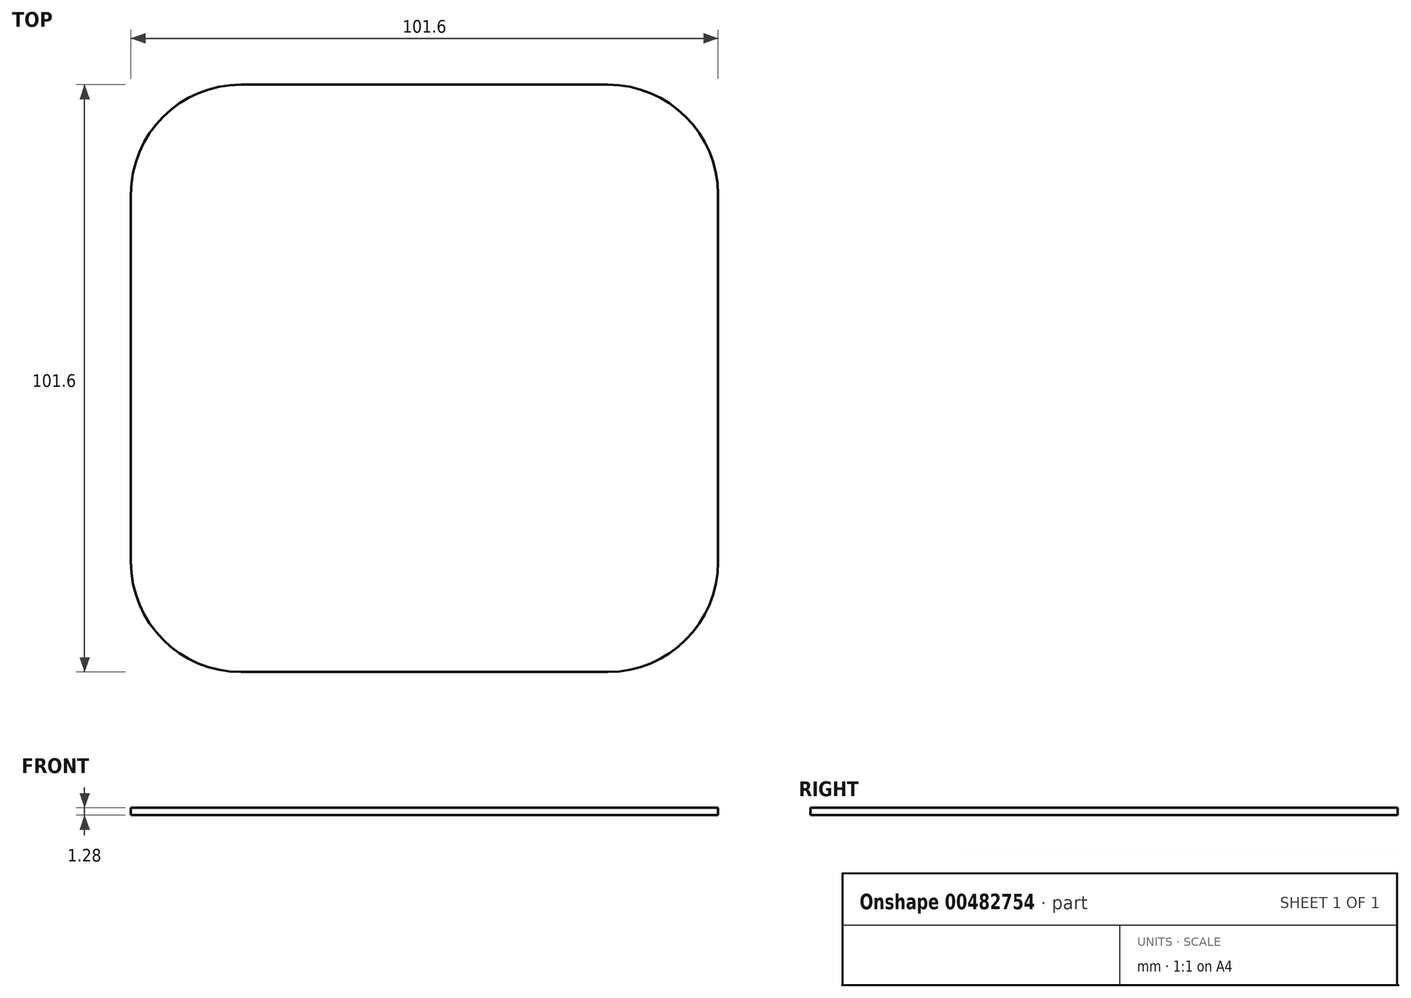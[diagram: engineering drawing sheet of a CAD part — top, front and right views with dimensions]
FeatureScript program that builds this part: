
annotation { "Feature Type Name" : "Feature", "Feature Type Description" : "" }
export const myFeature = defineFeature(function(context is Context, id is Id, definition is map)
    precondition{}
    {
        {
            var Q0;
            Q0=qCreatedBy(makeId("Top.planeOp"),FACE);
            var sketch = newSketch(context, id + "F0", { "sketchPlane" : qUnion([Q0])});
            skLineSegment(sketch, "E0.bottom", {"start": v(31.75, -50.8) * mm, "end": v(-31.75, -50.8) * mm});
            skLineSegment(sketch, "E0.top", {"start": v(31.75, 50.8) * mm, "end": v(-31.75, 50.8) * mm});
            skLineSegment(sketch, "E0.left", {"start": v(50.8, -31.75) * mm, "end": v(50.8, 31.75) * mm});
            skLineSegment(sketch, "E0.right", {"start": v(-50.8, -31.75) * mm, "end": v(-50.8, 31.75) * mm});
            skPoint(sketch, "E0.middle", {"position": v(0, 0) * mm});
            skPoint(sketch, "E1.visualSharp", {"position": v(-50.8, -50.8) * mm});
            skArc(sketch, "E1.filletArc", {"start": v(-50.8, -31.75) * mm, "mid": v(-45.22, -45.22) * mm, "end": v(-31.75, -50.8) * mm});
            skPoint(sketch, "E2.visualSharp", {"position": v(50.8, -50.8) * mm});
            skArc(sketch, "E2.filletArc", {"start": v(31.75, -50.8) * mm, "mid": v(45.22, -45.22) * mm, "end": v(50.8, -31.75) * mm});
            skPoint(sketch, "E3.visualSharp", {"position": v(50.8, 50.8) * mm});
            skArc(sketch, "E3.filletArc", {"start": v(50.8, 31.75) * mm, "mid": v(45.22, 45.22) * mm, "end": v(31.75, 50.8) * mm});
            skPoint(sketch, "E4.visualSharp", {"position": v(-50.8, 50.8) * mm});
            skArc(sketch, "E4.filletArc", {"start": v(-31.75, 50.8) * mm, "mid": v(-45.22, 45.22) * mm, "end": v(-50.8, 31.75) * mm});
            skSolve(sketch);
        }
        {
            var Q0;
            Q0 = qSketchRegion(id + "F0", true);
            extrude(context, id + "F1", {"entities" : qUnion([Q0]), "endBound" : BoundingType.SYMMETRIC, "depth" : 1.27 * mm});
        }
    });
